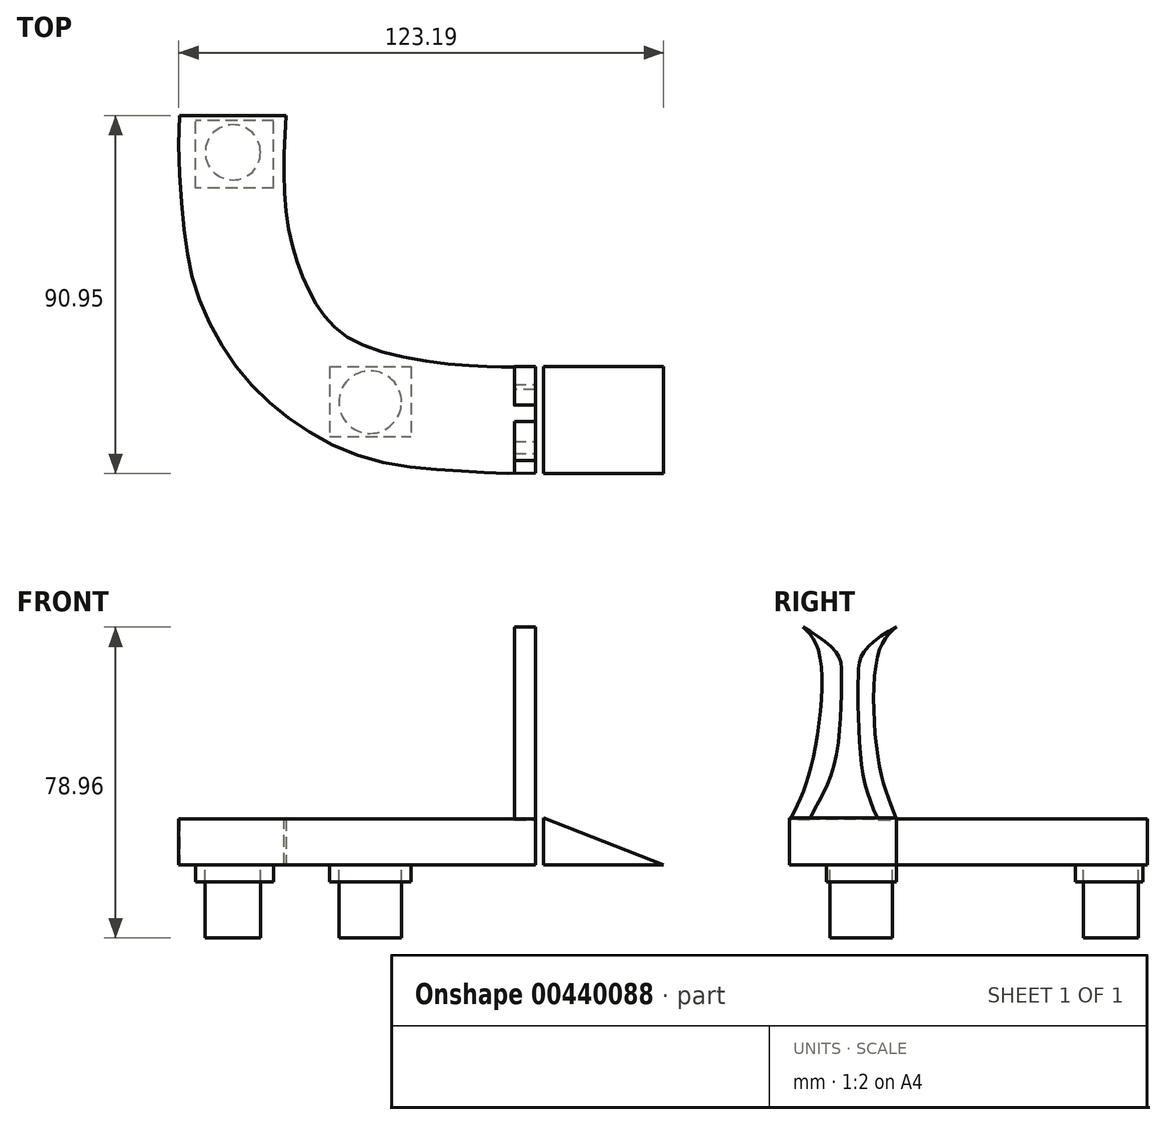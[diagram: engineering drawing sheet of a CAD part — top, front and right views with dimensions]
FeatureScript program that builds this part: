
annotation { "Feature Type Name" : "Feature", "Feature Type Description" : "" }
export const myFeature = defineFeature(function(context is Context, id is Id, definition is map)
    precondition{}
    {
        {
            var Q0;
            Q0=qCreatedBy(makeId("Top.planeOp"),FACE);
            var sketch = newSketch(context, id + "F0", { "sketchPlane" : qUnion([Q0])});
            skLineSegment(sketch, "E0.bottom", {"start": v(-66.47, 45.42) * mm, "end": v(-86.33, 45.42) * mm});
            skLineSegment(sketch, "E0.top", {"start": v(-66.47, 62.56) * mm, "end": v(-86.33, 62.56) * mm});
            skLineSegment(sketch, "E0.left", {"start": v(-66.47, 45.42) * mm, "end": v(-66.47, 62.56) * mm});
            skLineSegment(sketch, "E0.right", {"start": v(-86.33, 45.42) * mm, "end": v(-86.33, 62.56) * mm});
            skLineSegment(sketch, "E1.bottom", {"start": v(-52.34, 0) * mm, "end": v(-31.58, 0) * mm});
            skLineSegment(sketch, "E1.top", {"start": v(-52.34, -17.75) * mm, "end": v(-31.58, -17.75) * mm});
            skLineSegment(sketch, "E1.left", {"start": v(-52.34, 0) * mm, "end": v(-52.34, -17.75) * mm});
            skLineSegment(sketch, "E1.right", {"start": v(-31.58, 0) * mm, "end": v(-31.58, -17.75) * mm});
            skCircle(sketch, "E2", {"center": v(-76.4, 54) * mm, "radius": 7.19 * mm, "construction": true});
            skPoint(sketch, "E2.centerSnap0", {"position": v(-86.33, 54) * mm});
            skSolve(sketch);
        }
        {
            var Q0;
            Q0=makeQuery(id+"F0.imprint","IMPRINT",FACE,{"disambiguationData":[TD([[makeQuery(id+"F0.imprint","IMPRINT",EDGE,{"derivedFrom":sQuery(id+"F0.wireOp",EDGE,"tlbIkL3U-yA6t-6w48-x0YX-BTqFA8aSKLgz.bottom")}),-1.0]])]});
            var Q1;
            Q1=makeQuery(id+"F0.imprint","IMPRINT",FACE,{"disambiguationData":[TD([[makeQuery(id+"F0.imprint","IMPRINT",EDGE,{"derivedFrom":sQuery(id+"F0.wireOp",EDGE,"E0.bottom")}),-1.0]])]});
            var Q2;
            Q2=makeQuery(id+"F0.imprint","IMPRINT",FACE,{"disambiguationData":[TD([[makeQuery(id+"F0.imprint","IMPRINT",EDGE,{"derivedFrom":sQuery(id+"F0.wireOp",EDGE,"E1.bottom")}),-1.0]])]});
            var Q3;
            Q3=makeQuery(id+"F0.imprint","IMPRINT",FACE,{"disambiguationData":[TD([[makeQuery(id+"F0.imprint","IMPRINT",EDGE,{"derivedFrom":sQuery(id+"F0.wireOp",EDGE,"NKKlpAzA-O6YV-adBg-srxu-N7Sgs1YeVKqH.bottom")}),-1.0]])]});
            extrude(context, id + "F1", {"entities" : qUnion([Q0, Q1, Q2, Q3]), "oppositeDirection" : true, "depth" : 4.32 * mm});
        }
        {
            var Q0;
            Q0=qCreatedBy(makeId("Top.planeOp"),FACE);
            var sketch = newSketch(context, id + "F2", { "sketchPlane" : qUnion([Q0])});
            skCircle(sketch, "E3", {"center": v(-76.85, 54.44) * mm, "radius": 7.02 * mm});
            skSolve(sketch);
        }
        {
            var Q0;
            Q0 = qSketchRegion(id + "F2", true);
            extrude(context, id + "F3", {"entities" : qUnion([Q0]), "oppositeDirection" : true, "depth" : 18.54 * mm});
        }
        {
            var Q0;
            Q0=qCreatedBy(makeId("Top.planeOp"),FACE);
            var sketch = newSketch(context, id + "F4", { "sketchPlane" : qUnion([Q0])});
            skCircle(sketch, "E4", {"center": v(-41.96, -9.02) * mm, "radius": 7.95 * mm});
            skSolve(sketch);
        }
        {
            var Q0;
            Q0 = qSketchRegion(id + "F4", true);
            extrude(context, id + "F5", {"entities" : qUnion([Q0]), "oppositeDirection" : true, "depth" : 18.54 * mm});
        }
        {
            var Q0;
            Q0=qCreatedBy(makeId("Top.planeOp"),FACE);
            var sketch = newSketch(context, id + "F6", { "sketchPlane" : qUnion([Q0])});
            skFitSpline(sketch, "E5", {"points": [v(-90.42, 63.77) * mm, v(-89.44, 36.97) * mm, v(-85.82, 18.35) * mm, v(-75.95, 0) * mm, v(-61.96, -13.5) * mm, v(-42.26, -23.46) * mm, v(-19.7, -26.47) * mm, v(0, -27.07) * mm], "startDerivative": vector(-9.82, -165.02) * mm, "endDerivative": vector(178.1, 7.05) * mm});
            skFitSpline(sketch, "E6", {"points": [v(-63.32, 63.77) * mm, v(-63.02, 36.97) * mm, v(-57, 18.35) * mm, v(-44.97, 6.02) * mm, v(-13.08, 0) * mm, v(0, 0) * mm], "startDerivative": vector(-7.76, -117.1) * mm, "endDerivative": vector(83.43, 0) * mm});
            skLineSegment(sketch, "E7", {"start": v(-90.42, 63.77) * mm, "end": v(-63.32, 63.77) * mm});
            skLineSegment(sketch, "E8", {"start": v(0, -27.07) * mm, "end": v(0, 0) * mm});
            skFitSpline(sketch, "E9.MirrorCS", {"points": [v(63.32, 63.77) * mm, v(63.02, 36.97) * mm, v(57, 18.35) * mm, v(44.97, 6.02) * mm, v(13.08, 0) * mm, v(0, 0) * mm], "startDerivative": vector(7.76, -117.1) * mm, "endDerivative": vector(-83.43, 0) * mm});
            skFitSpline(sketch, "E10.MirrorCS", {"points": [v(90.42, 63.77) * mm, v(89.44, 36.97) * mm, v(85.82, 18.35) * mm, v(75.95, 0) * mm, v(61.96, -13.5) * mm, v(42.26, -23.46) * mm, v(19.7, -26.47) * mm, v(0, -27.07) * mm], "startDerivative": vector(9.82, -165.02) * mm, "endDerivative": vector(-178.1, 7.05) * mm});
            skLineSegment(sketch, "E11.MirrorCS", {"start": v(90.42, 63.77) * mm, "end": v(63.32, 63.77) * mm});
            skSolve(sketch);
        }
        {
            var Q0;
            Q0=makeQuery(id+"F6.imprint","IMPRINT",FACE,{"disambiguationData":[TD([[makeQuery(id+"F6.imprint","IMPRINT",EDGE,{"derivedFrom":sQuery(id+"F6.wireOp",EDGE,"E5")}),1.0]])]});
            extrude(context, id + "F7", {"entities" : qUnion([Q0]), "depth" : 11.68 * mm});
        }
        {
            var Q0;
            Q0=qCreatedBy(makeId("Right.planeOp"),FACE);
            var sketch = newSketch(context, id + "F8", { "sketchPlane" : qUnion([Q0])});
            skFitSpline(sketch, "E12", {"points": [v(-27, 11.42) * mm, v(-21.55, 25.47) * mm, v(-19.64, 53.75) * mm, v(-23.83, 60.42) * mm], "startDerivative": vector(19.37, 38.96) * mm, "endDerivative": vector(-22.3, 19.09) * mm});
            skFitSpline(sketch, "E13", {"points": [v(0, 11.42) * mm, v(-4.4, 25.47) * mm, v(-4.6, 53.75) * mm, v(0, 60.42) * mm], "startDerivative": vector(-14.6, 39.81) * mm, "endDerivative": vector(23.35, 18.46) * mm});
            skFitSpline(sketch, "E14", {"points": [v(-23.83, 60.42) * mm, v(-15.12, 53.75) * mm, v(-13.95, 47.1) * mm, v(-15.82, 25.47) * mm, v(-22.1, 11.42) * mm], "startDerivative": vector(45.4, -24.72) * mm, "endDerivative": vector(-24, -52.8) * mm});
            skFitSpline(sketch, "E15", {"points": [v(0, 60.42) * mm, v(-8.51, 53.75) * mm, v(-9.74, 47.1) * mm, v(-8.9, 25.47) * mm, v(-4.6, 11.42) * mm], "startDerivative": vector(-50.4, -23.74) * mm, "endDerivative": vector(25.2, -53.33) * mm});
            skLineSegment(sketch, "E16", {"start": v(-22.1, 11.42) * mm, "end": v(-27, 11.42) * mm});
            skLineSegment(sketch, "E17", {"start": v(-4.6, 11.42) * mm, "end": v(0, 11.42) * mm});
            skSolve(sketch);
        }
        {
            var Q0;
            Q0 = qSketchRegion(id + "F8", true);
            extrude(context, id + "F9", {"entities" : qUnion([Q0]), "oppositeDirection" : true, "depth" : 5.33 * mm});
        }
        {
            var Q0;
            Q0=qCreatedBy(makeId("Front.planeOp"),FACE);
            var sketch = newSketch(context, id + "F10", { "sketchPlane" : qUnion([Q0])});
            skLineSegment(sketch, "E18", {"start": v(2.1, 11.9) * mm, "end": v(32.58, 0) * mm});
            skLineSegment(sketch, "E19", {"start": v(32.58, 0) * mm, "end": v(2.1, 0) * mm});
            skLineSegment(sketch, "E20", {"start": v(2.1, 11.9) * mm, "end": v(2.1, 0) * mm});
            skSolve(sketch);
        }
        {
            var Q0;
            Q0=makeQuery(id+"F10.imprint","IMPRINT",FACE,{"disambiguationData":[TD([[makeQuery(id+"F10.imprint","IMPRINT",EDGE,{"derivedFrom":sQuery(id+"F10.wireOp",EDGE,"E18")}),-1.0]])]});
            extrude(context, id + "F11", {"entities" : qUnion([Q0]), "depth" : 27.18 * mm});
        }
    });
